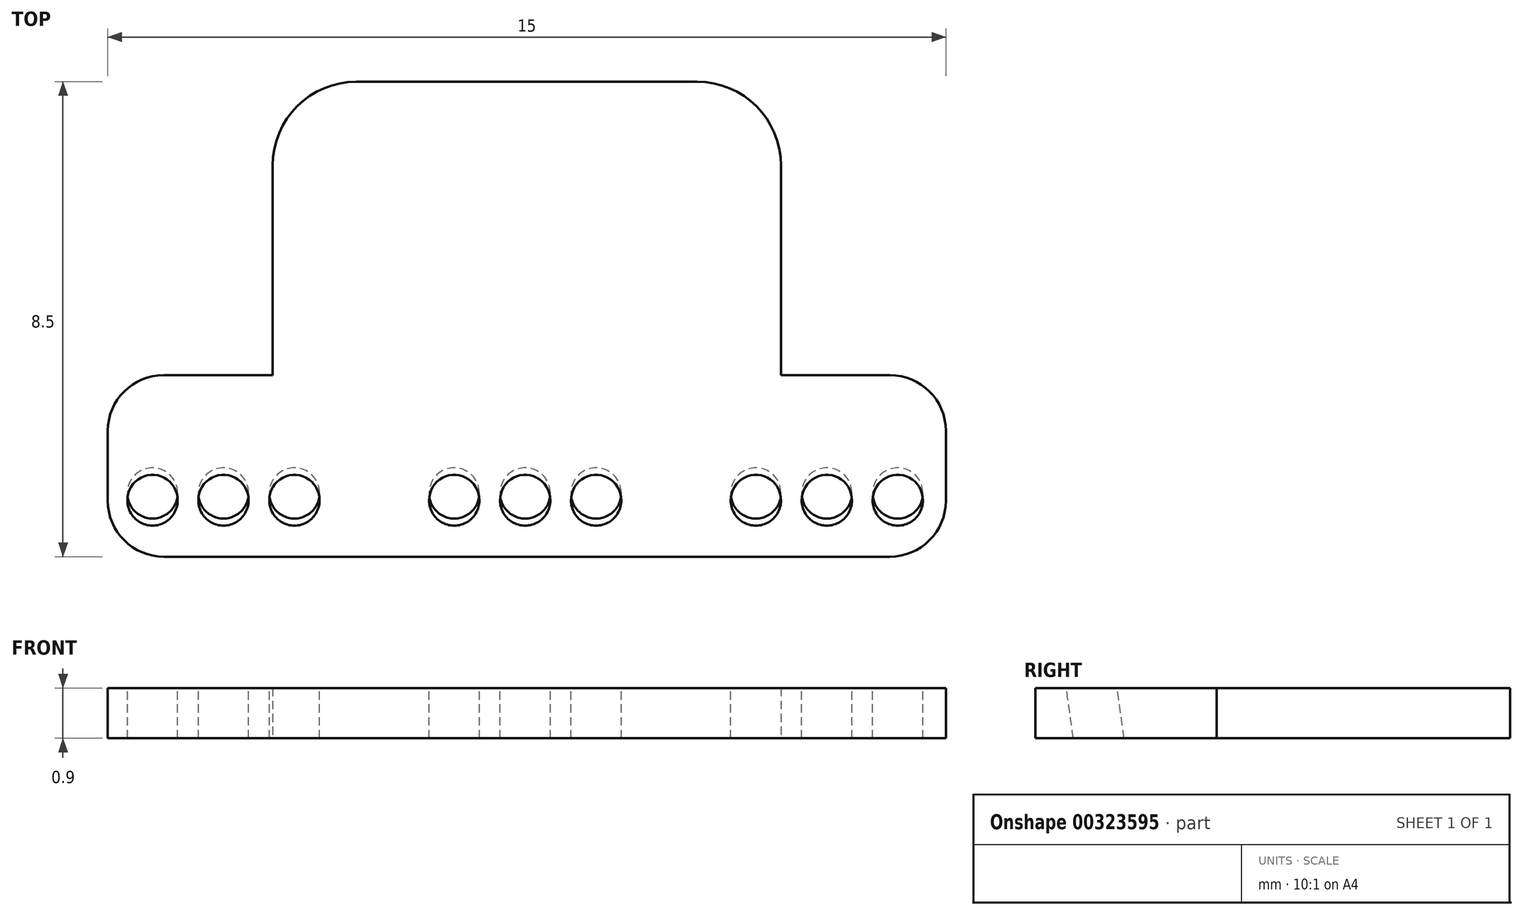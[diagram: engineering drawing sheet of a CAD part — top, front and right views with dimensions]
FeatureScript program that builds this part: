
annotation { "Feature Type Name" : "Feature", "Feature Type Description" : "" }
export const myFeature = defineFeature(function(context is Context, id is Id, definition is map)
    precondition{}
    {
        {
            var Q0;
            Q0=qCreatedBy(makeId("Top.planeOp"),FACE);
            var sketch = newSketch(context, id + "F0", { "sketchPlane" : qUnion([Q0])});
            skLineSegment(sketch, "E0.bottom", {"start": v(1, 0) * mm, "end": v(14, 0) * mm});
            skLineSegment(sketch, "E0.top", {"start": v(1, 3.25) * mm, "end": v(2.95, 3.25) * mm});
            skLineSegment(sketch, "E0.left", {"start": v(0, 1) * mm, "end": v(0, 2.25) * mm});
            skLineSegment(sketch, "E0.right", {"start": v(15, 1) * mm, "end": v(15, 2.25) * mm});
            skPoint(sketch, "E1.visualSharp", {"position": v(15, 0) * mm});
            skArc(sketch, "E1.filletArc", {"start": v(14, 0) * mm, "mid": v(14.7, 0.3) * mm, "end": v(15, 1) * mm});
            skPoint(sketch, "E2.visualSharp", {"position": v(15, 3.25) * mm});
            skArc(sketch, "E2.filletArc", {"start": v(15, 2.25) * mm, "mid": v(14.7, 2.96) * mm, "end": v(14, 3.25) * mm});
            skPoint(sketch, "E3.visualSharp", {"position": v(0, 0) * mm});
            skArc(sketch, "E3.filletArc", {"start": v(0, 1) * mm, "mid": v(0.3, 0.3) * mm, "end": v(1, 0) * mm});
            skPoint(sketch, "E4.visualSharp", {"position": v(0, 3.25) * mm});
            skArc(sketch, "E4.filletArc", {"start": v(1, 3.25) * mm, "mid": v(0.3, 2.96) * mm, "end": v(0, 2.25) * mm});
            skLineSegment(sketch, "E5.top", {"start": v(4.45, 8.5) * mm, "end": v(10.55, 8.5) * mm});
            skLineSegment(sketch, "E5.left", {"start": v(2.95, 3.25) * mm, "end": v(2.95, 7) * mm});
            skLineSegment(sketch, "E5.right", {"start": v(12.05, 3.25) * mm, "end": v(12.05, 7) * mm});
            skLineSegment(sketch, "E6.trimOffspring", {"start": v(12.05, 3.25) * mm, "end": v(14, 3.25) * mm});
            skPoint(sketch, "E7.visualSharp", {"position": v(2.95, 8.5) * mm});
            skArc(sketch, "E7.filletArc", {"start": v(4.45, 8.5) * mm, "mid": v(3.39, 8.06) * mm, "end": v(2.95, 7) * mm});
            skPoint(sketch, "E8.visualSharp", {"position": v(12.05, 8.5) * mm});
            skArc(sketch, "E8.filletArc", {"start": v(12.05, 7) * mm, "mid": v(11.61, 8.06) * mm, "end": v(10.55, 8.5) * mm});
            skSolve(sketch);
        }
        {
            var Q0;
            Q0 = qSketchRegion(id + "F0", true);
            extrude(context, id + "F1", {"entities" : qUnion([Q0]), "depth" : .9 * mm});
        }
        {
            var Q0;
            Q0=makeQuery(id+"F1.opExtrude","CAP_EDGE",EDGE,{"disambiguationData":[OSD([sQuery(id+"F0.wireOp",EDGE,"E0.bottom")])],"isStart":false});
            cPlane(context, id + "F2", {"entities" : qUnion([Q0]), "cplaneType" : CPlaneType.LINE_ANGLE, "offset" : 25 * mm, "angle" : 82 * degree, "oppositeDirection" : true, "width" : 150 * mm, "height" : 150 * mm});
        }
        {
            var Q0;
            Q0=qCreatedBy(id+"F2.planeOp",FACE);
            var sketch = newSketch(context, id + "F3", { "sketchPlane" : qUnion([Q0])});
            skCircle(sketch, "E9", {"center": v(0.8, -1.13) * mm, "radius": 0.45 * mm});
            skCircle(sketch, "E10", {"center": v(2.07, -1.13) * mm, "radius": 0.45 * mm});
            skCircle(sketch, "E11", {"center": v(3.34, -1.13) * mm, "radius": 0.45 * mm});
            skCircle(sketch, "E12.1.0.0", {"center": v(6.2, -1.13) * mm, "radius": 0.45 * mm});
            skCircle(sketch, "E12.1.0.1", {"center": v(7.47, -1.13) * mm, "radius": 0.45 * mm});
            skCircle(sketch, "E12.1.0.2", {"center": v(8.74, -1.13) * mm, "radius": 0.45 * mm});
            skCircle(sketch, "E12.2.0.0", {"center": v(11.6, -1.13) * mm, "radius": 0.45 * mm});
            skCircle(sketch, "E12.2.0.1", {"center": v(12.87, -1.13) * mm, "radius": 0.45 * mm});
            skCircle(sketch, "E12.2.0.2", {"center": v(14.14, -1.13) * mm, "radius": 0.45 * mm});
            skLineSegment(sketch, "E12.direction1", {"start": v(0.8, -1.13) * mm, "end": v(6.2, -1.13) * mm, "construction": true});
            skSolve(sketch);
        }
        {
            var Q0;
            Q0 = qSketchRegion(id + "F3", true);
            extrude(context, id + "F4", {"entities" : qUnion([Q0]), "operationType" : NewBodyOperationType.REMOVE, "depth" : 25 * mm});
        }
    });
